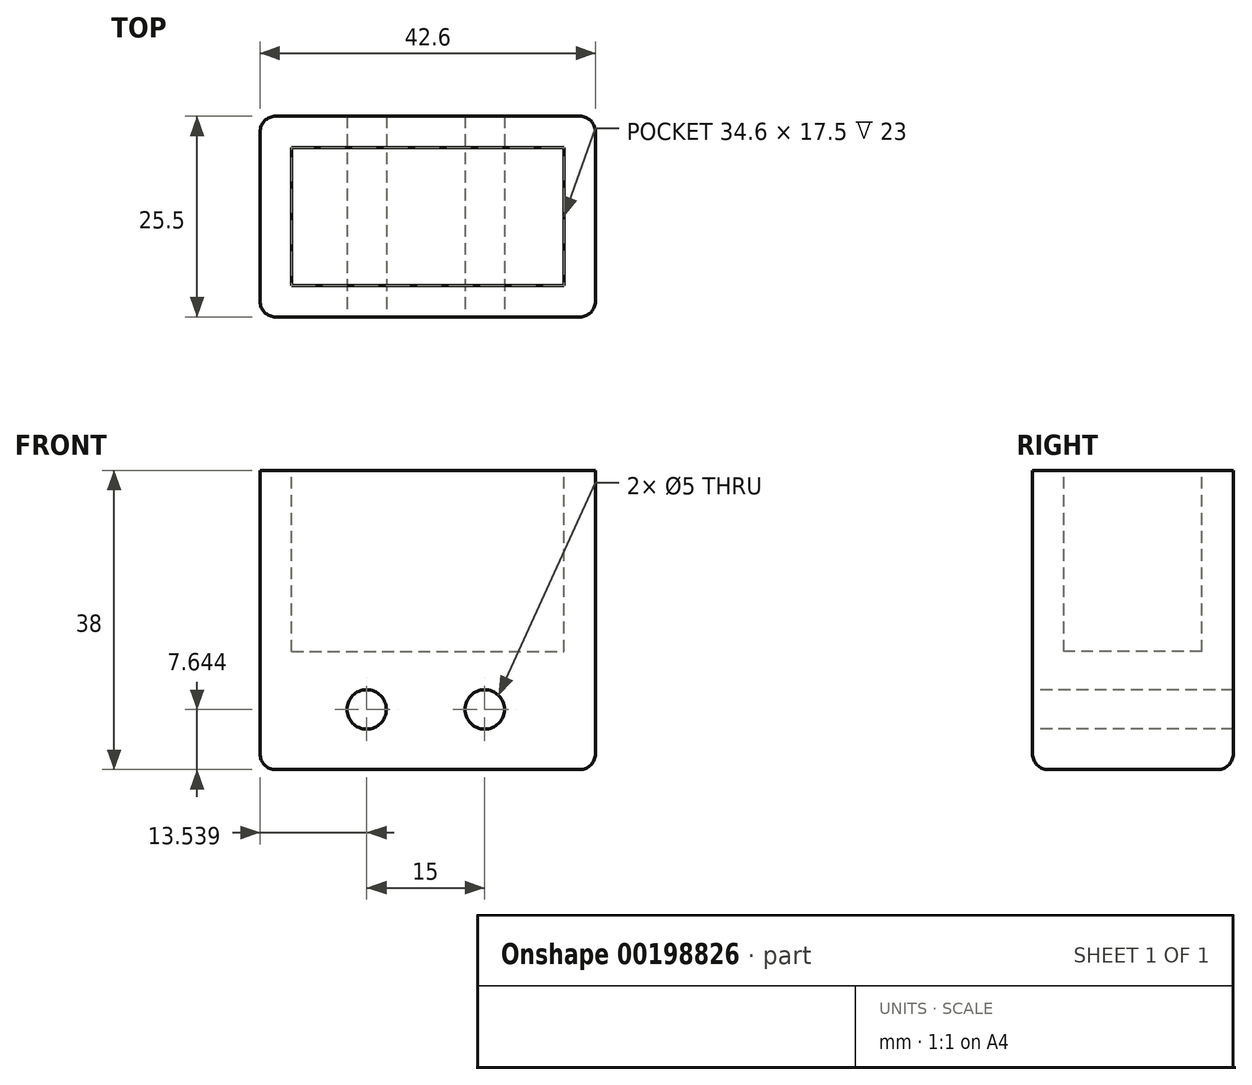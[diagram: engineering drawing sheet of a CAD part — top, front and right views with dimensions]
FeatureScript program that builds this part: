
annotation { "Feature Type Name" : "Feature", "Feature Type Description" : "" }
export const myFeature = defineFeature(function(context is Context, id is Id, definition is map)
    precondition{}
    {
        {
            var Q0;
            Q0=qCreatedBy(makeId("Top.planeOp"),FACE);
            var sketch = newSketch(context, id + "F0", { "sketchPlane" : qUnion([Q0])});
            skLineSegment(sketch, "E0.bottom", {"start": v(0, 17.5) * mm, "end": v(34.6, 17.5) * mm});
            skLineSegment(sketch, "E0.top", {"start": v(0, 0) * mm, "end": v(34.6, 0) * mm});
            skLineSegment(sketch, "E0.left", {"start": v(0, 17.5) * mm, "end": v(0, 0) * mm});
            skLineSegment(sketch, "E0.right", {"start": v(34.6, 17.5) * mm, "end": v(34.6, 0) * mm});
            skLineSegment(sketch, "E1.0", {"start": v(-2, 21.5) * mm, "end": v(36.6, 21.5) * mm});
            skLineSegment(sketch, "E1.1", {"start": v(-4, 19.5) * mm, "end": v(-4, -2) * mm});
            skLineSegment(sketch, "E1.2", {"start": v(-2, -4) * mm, "end": v(36.6, -4) * mm});
            skLineSegment(sketch, "E1.3", {"start": v(38.6, 19.5) * mm, "end": v(38.6, -2) * mm});
            skPoint(sketch, "E2.visualSharp", {"position": v(-4, 21.5) * mm});
            skArc(sketch, "E2.filletArc", {"start": v(-2, 21.5) * mm, "mid": v(-3.41, 20.91) * mm, "end": v(-4, 19.5) * mm});
            skPoint(sketch, "E3.visualSharp", {"position": v(38.6, 21.5) * mm});
            skArc(sketch, "E3.filletArc", {"start": v(38.6, 19.5) * mm, "mid": v(38.01, 20.91) * mm, "end": v(36.6, 21.5) * mm});
            skPoint(sketch, "E4.visualSharp", {"position": v(38.6, -4) * mm});
            skArc(sketch, "E4.filletArc", {"start": v(36.6, -4) * mm, "mid": v(38.01, -3.41) * mm, "end": v(38.6, -2) * mm});
            skPoint(sketch, "E5.visualSharp", {"position": v(-4, -4) * mm});
            skArc(sketch, "E5.filletArc", {"start": v(-4, -2) * mm, "mid": v(-3.41, -3.41) * mm, "end": v(-2, -4) * mm});
            skSolve(sketch);
        }
        {
            var Q0;
            Q0 = qSketchRegion(id + "F0", true);
            var Q1;
            Q1=makeQuery(id+"F0.imprint","IMPRINT",FACE,{"disambiguationData":[TD([[makeQuery(id+"F0.imprint","IMPRINT",EDGE,{"derivedFrom":sQuery(id+"F0.wireOp",EDGE,"E0.bottom")}),-1.0]])]});
            extrude(context, id + "F1", {"entities" : qUnion([Q0, Q1]), "oppositeDirection" : true, "depth" : 38 * mm});
        }
        {
            var Q0;
            Q0=makeQuery(id+"F0.imprint","IMPRINT",FACE,{"disambiguationData":[TD([[makeQuery(id+"F0.imprint","IMPRINT",EDGE,{"derivedFrom":sQuery(id+"F0.wireOp",EDGE,"E0.bottom")}),-1.0]])]});
            extrude(context, id + "F2", {"entities" : qUnion([Q0]), "operationType" : NewBodyOperationType.REMOVE, "oppositeDirection" : true, "depth" : 23 * mm});
        }
        {
            var Q0;
            Q0=makeQuery(id+"F1.opExtrude","SWEPT_FACE",FACE,{"disambiguationData":[OSD([sQuery(id+"F0.wireOp",EDGE,"E1.2")])]});
            var sketch = newSketch(context, id + "F3", { "sketchPlane" : qUnion([Q0])});
            skCircle(sketch, "E6", {"center": v(24.54, -30.36) * mm, "radius": 2.5 * mm});
            skCircle(sketch, "E7", {"center": v(9.54, -30.36) * mm, "radius": 2.5 * mm});
            skLineSegment(sketch, "E8", {"start": v(9.54, -30.36) * mm, "end": v(24.54, -30.36) * mm});
            skLineSegment(sketch, "E9", {"start": v(17.04, -30.36) * mm, "end": v(16.52, -30.36) * mm});
            skLineSegment(sketch, "E10", {"start": v(-2, 0) * mm, "end": v(36.6, 0) * mm});
            skLineSegment(sketch, "E11", {"start": v(17.04, -30.36) * mm, "end": v(17.04, -38) * mm});
            skLineSegment(sketch, "E12", {"start": v(17.04, -38) * mm, "end": v(17.04, -30.36) * mm});
            skLineSegment(sketch, "E13", {"start": v(17.04, -23) * mm, "end": v(17.04, -30.36) * mm});
            skLineSegment(sketch, "E14", {"start": v(17.04, -23) * mm, "end": v(17.04, 0) * mm});
            skSolve(sketch);
        }
        {
            var Q0;
            Q0 = qSketchRegion(id + "F3", true);
            extrude(context, id + "F4", {"entities" : qUnion([Q0]), "operationType" : NewBodyOperationType.REMOVE, "endBound" : BoundingType.THROUGH_ALL, "oppositeDirection" : true, "depth" : 28 * mm});
        }
        {
            var Q0;
            Q0=makeQuery(id+"F1.opExtrude","CAP_EDGE",EDGE,{"disambiguationData":[OSD([sQuery(id+"F0.wireOp",EDGE,"E1.0")])],"isStart":false});
            fillet(context, id + "F5", {"entities" : qUnion([Q0]), "radius" : 2 * mm, "tangentPropagation" : true, "allowEdgeOverflow" : false});
        }
    });
